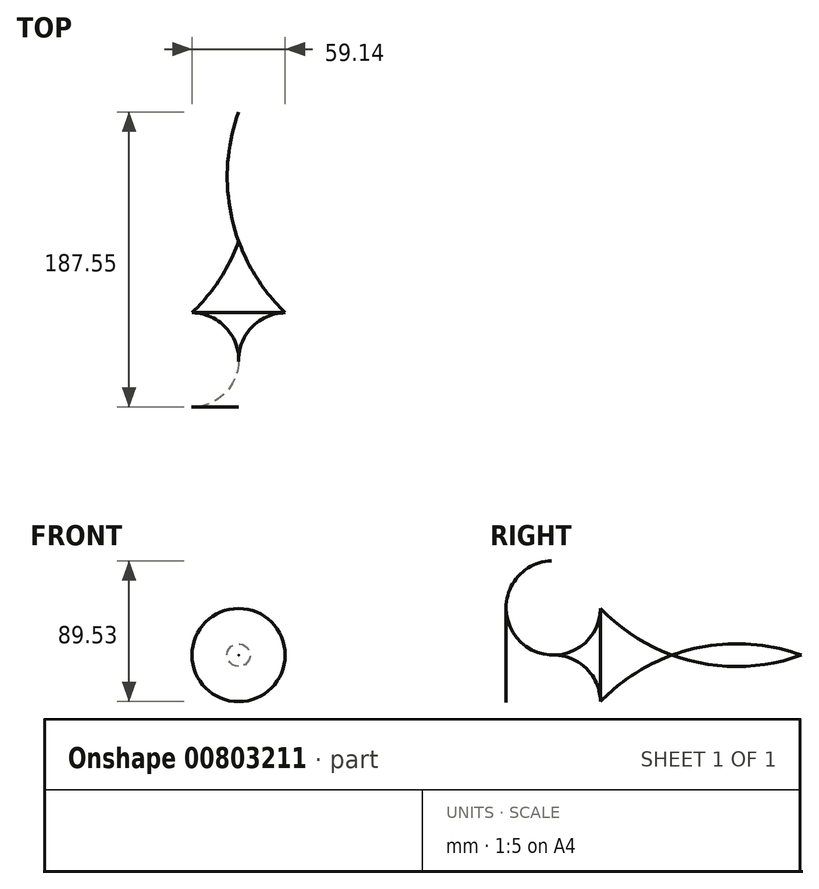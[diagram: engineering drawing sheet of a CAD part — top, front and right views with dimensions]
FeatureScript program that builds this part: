
annotation { "Feature Type Name" : "Feature", "Feature Type Description" : "" }
export const myFeature = defineFeature(function(context is Context, id is Id, definition is map)
    precondition{}
    {
        {
            var Q0;
            Q0=qCreatedBy(makeId("Top.planeOp"),FACE);
            var sketch = newSketch(context, id + "F0", { "sketchPlane" : qUnion([Q0])});
            skLineSegment(sketch, "E0", {"start": v(0, 83.8) * mm, "end": v(0, -85.61) * mm, "construction": true});
            skArc(sketch, "E1", {"start": v(29.57, 0) * mm, "mid": v(9.02, -8.53) * mm, "end": v(0, -28.87) * mm});
            skArc(sketch, "E2", {"start": v(0, 45.43) * mm, "mid": v(12.19, 21.02) * mm, "end": v(29.57, 0) * mm});
            skLineSegment(sketch, "E3", {"start": v(0, 45.43) * mm, "end": v(0, -28.87) * mm});
            skSolve(sketch);
        }
        {
            var Q0;
            Q0=makeQuery(id+"F0.imprint","IMPRINT",FACE,{"disambiguationData":[TD([[makeQuery(id+"F0.imprint","IMPRINT",EDGE,{"derivedFrom":sQuery(id+"F0.wireOp",EDGE,"E1")}),-1.0]])]});
            var Q1;
            Q1=sQuery(id+"F0.wireOp",EDGE,"E0");
            revolve(context, id + "F1", {"surfaceOperationType" : NewSurfaceOperationType.NEW, "entities" : qUnion([Q0]), "axis" : qUnion([Q1]), "revolveType" : RevolveType.FULL});
        }
    });
